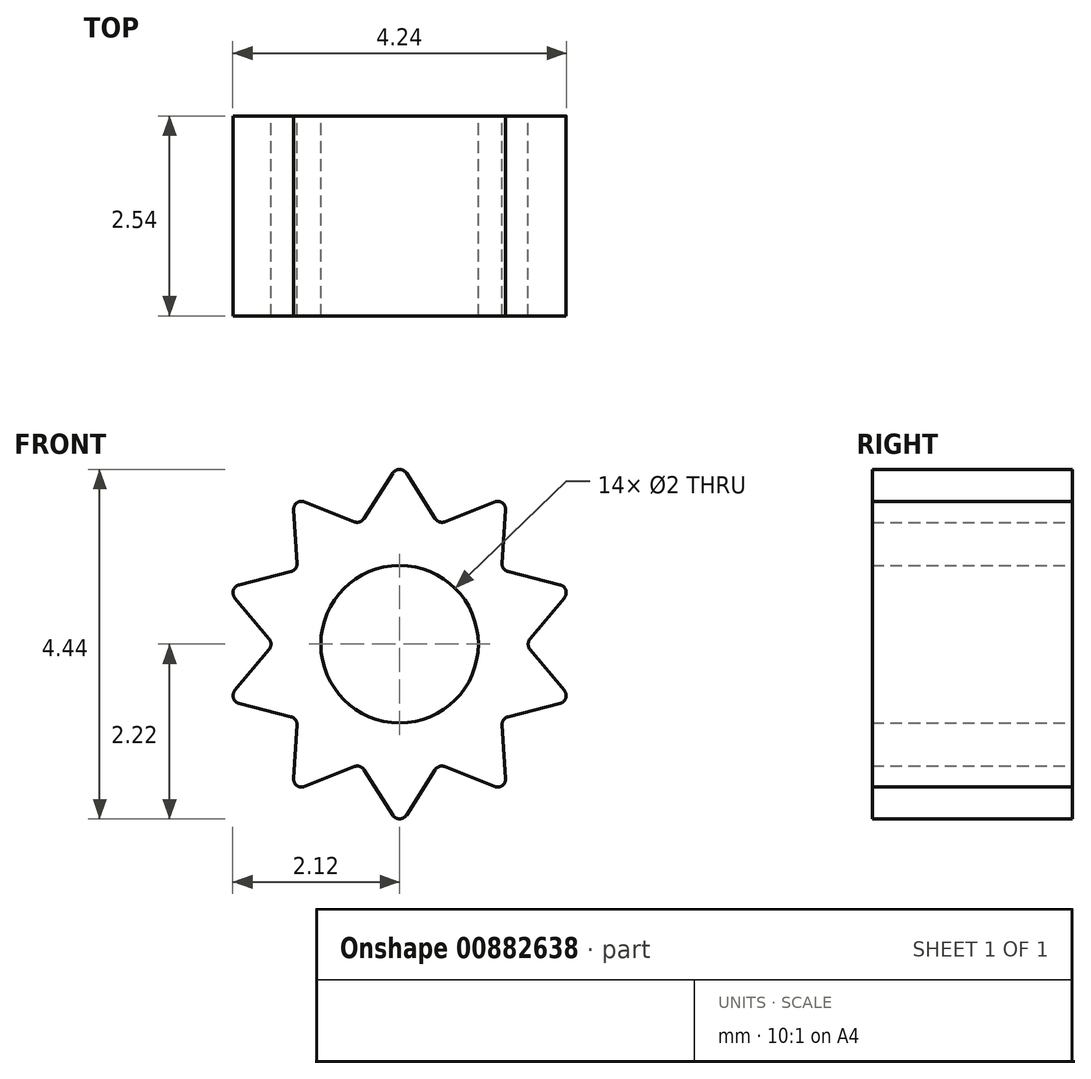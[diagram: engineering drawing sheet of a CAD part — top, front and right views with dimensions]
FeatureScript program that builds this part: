
annotation { "Feature Type Name" : "Feature", "Feature Type Description" : "" }
export const myFeature = defineFeature(function(context is Context, id is Id, definition is map)
    precondition{}
    {
        {
            var Q0;
            Q0=qCreatedBy(makeId("Front.planeOp"),FACE);
            var sketch = newSketch(context, id + "F0", { "sketchPlane" : qUnion([Q0])});
            skLineSegment(sketch, "E0", {"start": v(0, 0) * mm, "end": v(0, 1.59) * mm});
            skLineSegment(sketch, "E1", {"start": v(-0.5, 1.5) * mm, "end": v(0, 2.3) * mm});
            skLineSegment(sketch, "E2", {"start": v(0.5, 1.5) * mm, "end": v(0, 2.3) * mm});
            skPoint(sketch, "E3.end.orphan", {"position": v(0.5, 2.8) * mm});
            skPoint(sketch, "E4.end.orphan", {"position": v(-0.5, 2.8) * mm});
            skPoint(sketch, "E5.trimOffspring.start.orphan", {"position": v(0, 1.5) * mm});
            skLineSegment(sketch, "E6.1.0", {"start": v(-1.3, 0.92) * mm, "end": v(-1.36, 1.87) * mm});
            skLineSegment(sketch, "E6.1.1", {"start": v(-0.47, 1.52) * mm, "end": v(-1.36, 1.87) * mm});
            skLineSegment(sketch, "E6.2.0", {"start": v(-1.59, -0.02) * mm, "end": v(-2.2, 0.71) * mm});
            skLineSegment(sketch, "E6.2.1", {"start": v(-1.27, 0.95) * mm, "end": v(-2.2, 0.71) * mm});
            skLineSegment(sketch, "E6.3.0", {"start": v(-1.27, -0.95) * mm, "end": v(-2.2, -0.71) * mm});
            skLineSegment(sketch, "E6.3.1", {"start": v(-1.59, 0.02) * mm, "end": v(-2.2, -0.71) * mm});
            skLineSegment(sketch, "E6.4.0", {"start": v(-0.47, -1.52) * mm, "end": v(-1.36, -1.87) * mm});
            skLineSegment(sketch, "E6.4.1", {"start": v(-1.3, -0.92) * mm, "end": v(-1.36, -1.87) * mm});
            skLineSegment(sketch, "E6.5.0", {"start": v(0.5, -1.5) * mm, "end": v(0, -2.3) * mm});
            skLineSegment(sketch, "E6.5.1", {"start": v(-0.5, -1.5) * mm, "end": v(0, -2.3) * mm});
            skLineSegment(sketch, "E6.6.0", {"start": v(1.3, -0.92) * mm, "end": v(1.36, -1.87) * mm});
            skLineSegment(sketch, "E6.6.1", {"start": v(0.47, -1.52) * mm, "end": v(1.36, -1.87) * mm});
            skLineSegment(sketch, "E6.7.0", {"start": v(1.59, 0.02) * mm, "end": v(2.2, -0.71) * mm});
            skLineSegment(sketch, "E6.7.1", {"start": v(1.27, -0.95) * mm, "end": v(2.2, -0.71) * mm});
            skLineSegment(sketch, "E6.8.0", {"start": v(1.27, 0.95) * mm, "end": v(2.2, 0.71) * mm});
            skLineSegment(sketch, "E6.8.1", {"start": v(1.59, -0.02) * mm, "end": v(2.2, 0.71) * mm});
            skLineSegment(sketch, "E6.9.0", {"start": v(0.47, 1.52) * mm, "end": v(1.36, 1.87) * mm});
            skLineSegment(sketch, "E6.9.1", {"start": v(1.3, 0.92) * mm, "end": v(1.36, 1.87) * mm});
            skPoint(sketch, "E6.center", {"position": v(0, 0) * mm});
            skCircle(sketch, "E7", {"center": v(0, 0) * mm, "radius": 1 * mm});
            skSolve(sketch);
        }
        {
            var Q0;
            Q0=makeQuery(id+"F0.imprint","IMPRINT",FACE,{"disambiguationData":[TD([[makeQuery(id+"F0.imprint","IMPRINT",EDGE,{"derivedFrom":sQuery(id+"F0.wireOp",EDGE,"sXcNP9sW-BnGK-NUdi-REFe-XZlWx95a0Vfr")}),-1.0]])]});
            var Q1;
            {var subQ3=sQuery(id+"F0.wireOp",EDGE,"E1");var subQ7=sQuery(id+"F0.wireOp",EDGE,"FmjKioGj-E6GO-fnAS-C736-YH94ok3mVgz6");var subQ8=makeQuery(id+"F0.imprint","INTERSECT",VERTEX,{"derivedFrom":[subQ7,subQ3]});Q1=makeQuery(id+"F0.imprint","IMPRINT",FACE,{"disambiguationData":[TD([[makeQuery(id+"F0.imprint","IMPRINT",EDGE,{"disambiguationData":[TD([[subQ8,-1.0]])],"derivedFrom":subQ7}),-1.0]])]});}
            var Q2;
            {var subQ3=sQuery(id+"F0.wireOp",EDGE,"E6.1.0");var subQ7=sQuery(id+"F0.wireOp",EDGE,"FmjKioGj-E6GO-fnAS-C736-YH94ok3mVgz6");var subQ8=makeQuery(id+"F0.imprint","INTERSECT",VERTEX,{"derivedFrom":[subQ7,subQ3]});Q2=makeQuery(id+"F0.imprint","IMPRINT",FACE,{"disambiguationData":[TD([[makeQuery(id+"F0.imprint","IMPRINT",EDGE,{"disambiguationData":[TD([[subQ8,-1.0]])],"derivedFrom":subQ7}),-1.0]])]});}
            var Q3;
            {var subQ3=sQuery(id+"F0.wireOp",EDGE,"E6.2.0");var subQ7=sQuery(id+"F0.wireOp",EDGE,"FmjKioGj-E6GO-fnAS-C736-YH94ok3mVgz6");var subQ8=makeQuery(id+"F0.imprint","INTERSECT",VERTEX,{"derivedFrom":[subQ7,subQ3]});Q3=makeQuery(id+"F0.imprint","IMPRINT",FACE,{"disambiguationData":[TD([[makeQuery(id+"F0.imprint","IMPRINT",EDGE,{"disambiguationData":[TD([[subQ8,-1.0]])],"derivedFrom":subQ7}),-1.0]])]});}
            var Q4;
            {var subQ5=sQuery(id+"F0.wireOp",EDGE,"E6.3.0");var subQ6=sQuery(id+"F0.wireOp",EDGE,"FmjKioGj-E6GO-fnAS-C736-YH94ok3mVgz6");var subQ7=makeQuery(id+"F0.imprint","INTERSECT",VERTEX,{"derivedFrom":[subQ6,subQ5]});Q4=makeQuery(id+"F0.imprint","IMPRINT",FACE,{"disambiguationData":[TD([[makeQuery(id+"F0.imprint","IMPRINT",EDGE,{"disambiguationData":[TD([[subQ7,-1.0]])],"derivedFrom":subQ6}),-1.0]])]});}
            var Q5;
            {var subQ3=sQuery(id+"F0.wireOp",EDGE,"E6.4.0");var subQ7=sQuery(id+"F0.wireOp",EDGE,"FmjKioGj-E6GO-fnAS-C736-YH94ok3mVgz6");var subQ8=makeQuery(id+"F0.imprint","INTERSECT",VERTEX,{"derivedFrom":[subQ7,subQ3]});Q5=makeQuery(id+"F0.imprint","IMPRINT",FACE,{"disambiguationData":[TD([[makeQuery(id+"F0.imprint","IMPRINT",EDGE,{"disambiguationData":[TD([[subQ8,-1.0]])],"derivedFrom":subQ7}),-1.0]])]});}
            var Q6;
            {var subQ3=sQuery(id+"F0.wireOp",EDGE,"E6.5.0");var subQ7=sQuery(id+"F0.wireOp",EDGE,"FmjKioGj-E6GO-fnAS-C736-YH94ok3mVgz6");var subQ8=makeQuery(id+"F0.imprint","INTERSECT",VERTEX,{"derivedFrom":[subQ7,subQ3]});Q6=makeQuery(id+"F0.imprint","IMPRINT",FACE,{"disambiguationData":[TD([[makeQuery(id+"F0.imprint","IMPRINT",EDGE,{"disambiguationData":[TD([[subQ8,-1.0]])],"derivedFrom":subQ7}),-1.0]])]});}
            var Q7;
            {var subQ3=sQuery(id+"F0.wireOp",EDGE,"E6.6.0");var subQ7=sQuery(id+"F0.wireOp",EDGE,"FmjKioGj-E6GO-fnAS-C736-YH94ok3mVgz6");var subQ8=makeQuery(id+"F0.imprint","INTERSECT",VERTEX,{"derivedFrom":[subQ7,subQ3]});Q7=makeQuery(id+"F0.imprint","IMPRINT",FACE,{"disambiguationData":[TD([[makeQuery(id+"F0.imprint","IMPRINT",EDGE,{"disambiguationData":[TD([[subQ8,-1.0]])],"derivedFrom":subQ7}),-1.0]])]});}
            var Q8;
            {var subQ3=sQuery(id+"F0.wireOp",EDGE,"E6.7.0");var subQ7=sQuery(id+"F0.wireOp",EDGE,"FmjKioGj-E6GO-fnAS-C736-YH94ok3mVgz6");var subQ8=makeQuery(id+"F0.imprint","INTERSECT",VERTEX,{"derivedFrom":[subQ7,subQ3]});Q8=makeQuery(id+"F0.imprint","IMPRINT",FACE,{"disambiguationData":[TD([[makeQuery(id+"F0.imprint","IMPRINT",EDGE,{"disambiguationData":[TD([[subQ8,-1.0]])],"derivedFrom":subQ7}),-1.0]])]});}
            var Q9;
            {var subQ3=sQuery(id+"F0.wireOp",EDGE,"E2");var subQ6=sQuery(id+"F0.wireOp",EDGE,"FmjKioGj-E6GO-fnAS-C736-YH94ok3mVgz6");var subQ9=makeQuery(id+"F0.imprint","INTERSECT",VERTEX,{"derivedFrom":[subQ6,subQ3]});Q9=makeQuery(id+"F0.imprint","IMPRINT",FACE,{"disambiguationData":[TD([[makeQuery(id+"F0.imprint","IMPRINT",EDGE,{"disambiguationData":[TD([[subQ9,1.0]])],"derivedFrom":subQ6}),-1.0]])]});}
            var Q10;
            {var subQ3=sQuery(id+"F0.wireOp",EDGE,"E1");var subQ7=sQuery(id+"F0.wireOp",EDGE,"sXcNP9sW-BnGK-NUdi-REFe-XZlWx95a0Vfr");var subQ8=makeQuery(id+"F0.imprint","INTERSECT",VERTEX,{"derivedFrom":[subQ3,subQ7]});Q10=makeQuery(id+"F0.imprint","IMPRINT",FACE,{"disambiguationData":[TD([[makeQuery(id+"F0.imprint","IMPRINT",EDGE,{"disambiguationData":[TD([[subQ8,-1.0]])],"derivedFrom":subQ3}),1.0]])]});}
            var Q11;
            Q11=makeQuery(id+"F0.imprint","IMPRINT",FACE,{"disambiguationData":[TD([[makeQuery(id+"F0.imprint","IMPRINT",EDGE,{"derivedFrom":sQuery(id+"F0.wireOp",EDGE,"E7")}),-1.0]])]});
            var Q12;
            {var subQ3=sQuery(id+"F0.wireOp",EDGE,"E6.1.0");var subQ7=sQuery(id+"F0.wireOp",EDGE,"sXcNP9sW-BnGK-NUdi-REFe-XZlWx95a0Vfr");var subQ8=makeQuery(id+"F0.imprint","INTERSECT",VERTEX,{"derivedFrom":[subQ7,subQ3]});Q12=makeQuery(id+"F0.imprint","IMPRINT",FACE,{"disambiguationData":[TD([[makeQuery(id+"F0.imprint","IMPRINT",EDGE,{"disambiguationData":[TD([[subQ8,-1.0]])],"derivedFrom":subQ7}),-1.0]])]});}
            var Q13;
            {var subQ3=sQuery(id+"F0.wireOp",EDGE,"E6.2.0");var subQ7=sQuery(id+"F0.wireOp",EDGE,"sXcNP9sW-BnGK-NUdi-REFe-XZlWx95a0Vfr");var subQ8=makeQuery(id+"F0.imprint","INTERSECT",VERTEX,{"derivedFrom":[subQ7,subQ3]});Q13=makeQuery(id+"F0.imprint","IMPRINT",FACE,{"disambiguationData":[TD([[makeQuery(id+"F0.imprint","IMPRINT",EDGE,{"disambiguationData":[TD([[subQ8,-1.0]])],"derivedFrom":subQ7}),-1.0]])]});}
            var Q14;
            {var subQ3=sQuery(id+"F0.wireOp",EDGE,"E6.3.0");var subQ7=sQuery(id+"F0.wireOp",EDGE,"sXcNP9sW-BnGK-NUdi-REFe-XZlWx95a0Vfr");var subQ8=makeQuery(id+"F0.imprint","INTERSECT",VERTEX,{"derivedFrom":[subQ7,subQ3]});Q14=makeQuery(id+"F0.imprint","IMPRINT",FACE,{"disambiguationData":[TD([[makeQuery(id+"F0.imprint","IMPRINT",EDGE,{"disambiguationData":[TD([[subQ8,-1.0]])],"derivedFrom":subQ7}),-1.0]])]});}
            var Q15;
            {var subQ5=sQuery(id+"F0.wireOp",EDGE,"E6.4.0");var subQ6=sQuery(id+"F0.wireOp",EDGE,"sXcNP9sW-BnGK-NUdi-REFe-XZlWx95a0Vfr");var subQ7=makeQuery(id+"F0.imprint","INTERSECT",VERTEX,{"derivedFrom":[subQ6,subQ5]});Q15=makeQuery(id+"F0.imprint","IMPRINT",FACE,{"disambiguationData":[TD([[makeQuery(id+"F0.imprint","IMPRINT",EDGE,{"disambiguationData":[TD([[subQ7,-1.0]])],"derivedFrom":subQ6}),-1.0]])]});}
            var Q16;
            {var subQ3=sQuery(id+"F0.wireOp",EDGE,"E6.5.0");var subQ7=sQuery(id+"F0.wireOp",EDGE,"sXcNP9sW-BnGK-NUdi-REFe-XZlWx95a0Vfr");var subQ8=makeQuery(id+"F0.imprint","INTERSECT",VERTEX,{"derivedFrom":[subQ7,subQ3]});Q16=makeQuery(id+"F0.imprint","IMPRINT",FACE,{"disambiguationData":[TD([[makeQuery(id+"F0.imprint","IMPRINT",EDGE,{"disambiguationData":[TD([[subQ8,-1.0]])],"derivedFrom":subQ7}),-1.0]])]});}
            var Q17;
            {var subQ3=sQuery(id+"F0.wireOp",EDGE,"E6.6.0");var subQ7=sQuery(id+"F0.wireOp",EDGE,"sXcNP9sW-BnGK-NUdi-REFe-XZlWx95a0Vfr");var subQ8=makeQuery(id+"F0.imprint","INTERSECT",VERTEX,{"derivedFrom":[subQ7,subQ3]});Q17=makeQuery(id+"F0.imprint","IMPRINT",FACE,{"disambiguationData":[TD([[makeQuery(id+"F0.imprint","IMPRINT",EDGE,{"disambiguationData":[TD([[subQ8,-1.0]])],"derivedFrom":subQ7}),-1.0]])]});}
            var Q18;
            {var subQ3=sQuery(id+"F0.wireOp",EDGE,"E6.7.0");var subQ7=sQuery(id+"F0.wireOp",EDGE,"sXcNP9sW-BnGK-NUdi-REFe-XZlWx95a0Vfr");var subQ8=makeQuery(id+"F0.imprint","INTERSECT",VERTEX,{"derivedFrom":[subQ7,subQ3]});Q18=makeQuery(id+"F0.imprint","IMPRINT",FACE,{"disambiguationData":[TD([[makeQuery(id+"F0.imprint","IMPRINT",EDGE,{"disambiguationData":[TD([[subQ8,-1.0]])],"derivedFrom":subQ7}),-1.0]])]});}
            var Q19;
            {var subQ3=sQuery(id+"F0.wireOp",EDGE,"E2");var subQ6=sQuery(id+"F0.wireOp",EDGE,"sXcNP9sW-BnGK-NUdi-REFe-XZlWx95a0Vfr");var subQ9=makeQuery(id+"F0.imprint","INTERSECT",VERTEX,{"derivedFrom":[subQ3,subQ6]});Q19=makeQuery(id+"F0.imprint","IMPRINT",FACE,{"disambiguationData":[TD([[makeQuery(id+"F0.imprint","IMPRINT",EDGE,{"disambiguationData":[TD([[subQ9,-1.0]])],"derivedFrom":subQ3}),-1.0]])]});}
            extrude(context, id + "F1", {"entities" : qUnion([Q0, Q1, Q2, Q3, Q4, Q5, Q6, Q7, Q8, Q9, Q10, Q11, Q12, Q13, Q14, Q15, Q16, Q17, Q18, Q19]), "depth" : 2.54 * mm, "offsetDistance" : 25.4 * mm});
        }
        {
            var Q0;
            Q0=makeQuery(id+"F1.opExtrude","SWEPT_EDGE",EDGE,{"disambiguationData":[OSD([sQuery(id+"F0.wireOp",EDGE,"E1"),sQuery(id+"F0.wireOp",EDGE,"E2")])]});
            var Q1;
            Q1=makeQuery(id+"F1.opExtrude","SWEPT_EDGE",EDGE,{"disambiguationData":[OSD([sQuery(id+"F0.wireOp",EDGE,"E2"),sQuery(id+"F0.wireOp",EDGE,"E6.9.0")])]});
            var Q2;
            Q2=makeQuery(id+"F1.opExtrude","SWEPT_EDGE",EDGE,{"disambiguationData":[OSD([sQuery(id+"F0.wireOp",EDGE,"E6.9.0"),sQuery(id+"F0.wireOp",EDGE,"E6.9.1")])]});
            var Q3;
            Q3=makeQuery(id+"F1.opExtrude","SWEPT_EDGE",EDGE,{"disambiguationData":[OSD([sQuery(id+"F0.wireOp",EDGE,"E6.8.0"),sQuery(id+"F0.wireOp",EDGE,"E6.9.1")])]});
            var Q4;
            Q4=makeQuery(id+"F1.opExtrude","SWEPT_EDGE",EDGE,{"disambiguationData":[OSD([sQuery(id+"F0.wireOp",EDGE,"E6.8.0"),sQuery(id+"F0.wireOp",EDGE,"E6.8.1")])]});
            var Q5;
            Q5=makeQuery(id+"F1.opExtrude","SWEPT_EDGE",EDGE,{"disambiguationData":[OSD([sQuery(id+"F0.wireOp",EDGE,"E6.7.0"),sQuery(id+"F0.wireOp",EDGE,"E6.8.1")])]});
            var Q6;
            Q6=makeQuery(id+"F1.opExtrude","SWEPT_EDGE",EDGE,{"disambiguationData":[OSD([sQuery(id+"F0.wireOp",EDGE,"E6.7.0"),sQuery(id+"F0.wireOp",EDGE,"E6.7.1")])]});
            var Q7;
            Q7=makeQuery(id+"F1.opExtrude","SWEPT_EDGE",EDGE,{"disambiguationData":[OSD([sQuery(id+"F0.wireOp",EDGE,"E6.6.0"),sQuery(id+"F0.wireOp",EDGE,"E6.7.1")])]});
            var Q8;
            Q8=makeQuery(id+"F1.opExtrude","SWEPT_EDGE",EDGE,{"disambiguationData":[OSD([sQuery(id+"F0.wireOp",EDGE,"E6.6.0"),sQuery(id+"F0.wireOp",EDGE,"E6.6.1")])]});
            var Q9;
            Q9=makeQuery(id+"F1.opExtrude","SWEPT_EDGE",EDGE,{"disambiguationData":[OSD([sQuery(id+"F0.wireOp",EDGE,"E6.5.0"),sQuery(id+"F0.wireOp",EDGE,"E6.6.1")])]});
            var Q10;
            Q10=makeQuery(id+"F1.opExtrude","SWEPT_EDGE",EDGE,{"disambiguationData":[OSD([sQuery(id+"F0.wireOp",EDGE,"E6.5.0"),sQuery(id+"F0.wireOp",EDGE,"E6.5.1")])]});
            var Q11;
            Q11=makeQuery(id+"F1.opExtrude","SWEPT_EDGE",EDGE,{"disambiguationData":[OSD([sQuery(id+"F0.wireOp",EDGE,"E6.4.0"),sQuery(id+"F0.wireOp",EDGE,"E6.4.1")])]});
            var Q12;
            Q12=makeQuery(id+"F1.opExtrude","SWEPT_EDGE",EDGE,{"disambiguationData":[OSD([sQuery(id+"F0.wireOp",EDGE,"E6.4.0"),sQuery(id+"F0.wireOp",EDGE,"E6.5.1")])]});
            var Q13;
            Q13=makeQuery(id+"F1.opExtrude","SWEPT_EDGE",EDGE,{"disambiguationData":[OSD([sQuery(id+"F0.wireOp",EDGE,"E6.3.0"),sQuery(id+"F0.wireOp",EDGE,"E6.4.1")])]});
            var Q14;
            Q14=makeQuery(id+"F1.opExtrude","SWEPT_EDGE",EDGE,{"disambiguationData":[OSD([sQuery(id+"F0.wireOp",EDGE,"E6.3.0"),sQuery(id+"F0.wireOp",EDGE,"E6.3.1")])]});
            var Q15;
            Q15=makeQuery(id+"F1.opExtrude","SWEPT_EDGE",EDGE,{"disambiguationData":[OSD([sQuery(id+"F0.wireOp",EDGE,"E6.2.0"),sQuery(id+"F0.wireOp",EDGE,"E6.3.1")])]});
            var Q16;
            Q16=makeQuery(id+"F1.opExtrude","SWEPT_EDGE",EDGE,{"disambiguationData":[OSD([sQuery(id+"F0.wireOp",EDGE,"E6.2.0"),sQuery(id+"F0.wireOp",EDGE,"E6.2.1")])]});
            var Q17;
            Q17=makeQuery(id+"F1.opExtrude","SWEPT_EDGE",EDGE,{"disambiguationData":[OSD([sQuery(id+"F0.wireOp",EDGE,"E6.1.0"),sQuery(id+"F0.wireOp",EDGE,"E6.2.1")])]});
            var Q18;
            Q18=makeQuery(id+"F1.opExtrude","SWEPT_EDGE",EDGE,{"disambiguationData":[OSD([sQuery(id+"F0.wireOp",EDGE,"E6.1.0"),sQuery(id+"F0.wireOp",EDGE,"E6.1.1")])]});
            var Q19;
            Q19=makeQuery(id+"F1.opExtrude","SWEPT_EDGE",EDGE,{"disambiguationData":[OSD([sQuery(id+"F0.wireOp",EDGE,"E1"),sQuery(id+"F0.wireOp",EDGE,"E6.1.1")])]});
            fillet(context, id + "F2", {"entities" : qUnion([Q0, Q1, Q2, Q3, Q4, Q5, Q6, Q7, Q8, Q9, Q10, Q11, Q12, Q13, Q14, Q15, Q16, Q17, Q18, Q19]), "radius" : 0.1 * mm, "tangentPropagation" : true, "allowEdgeOverflow" : false});
        }
    });
